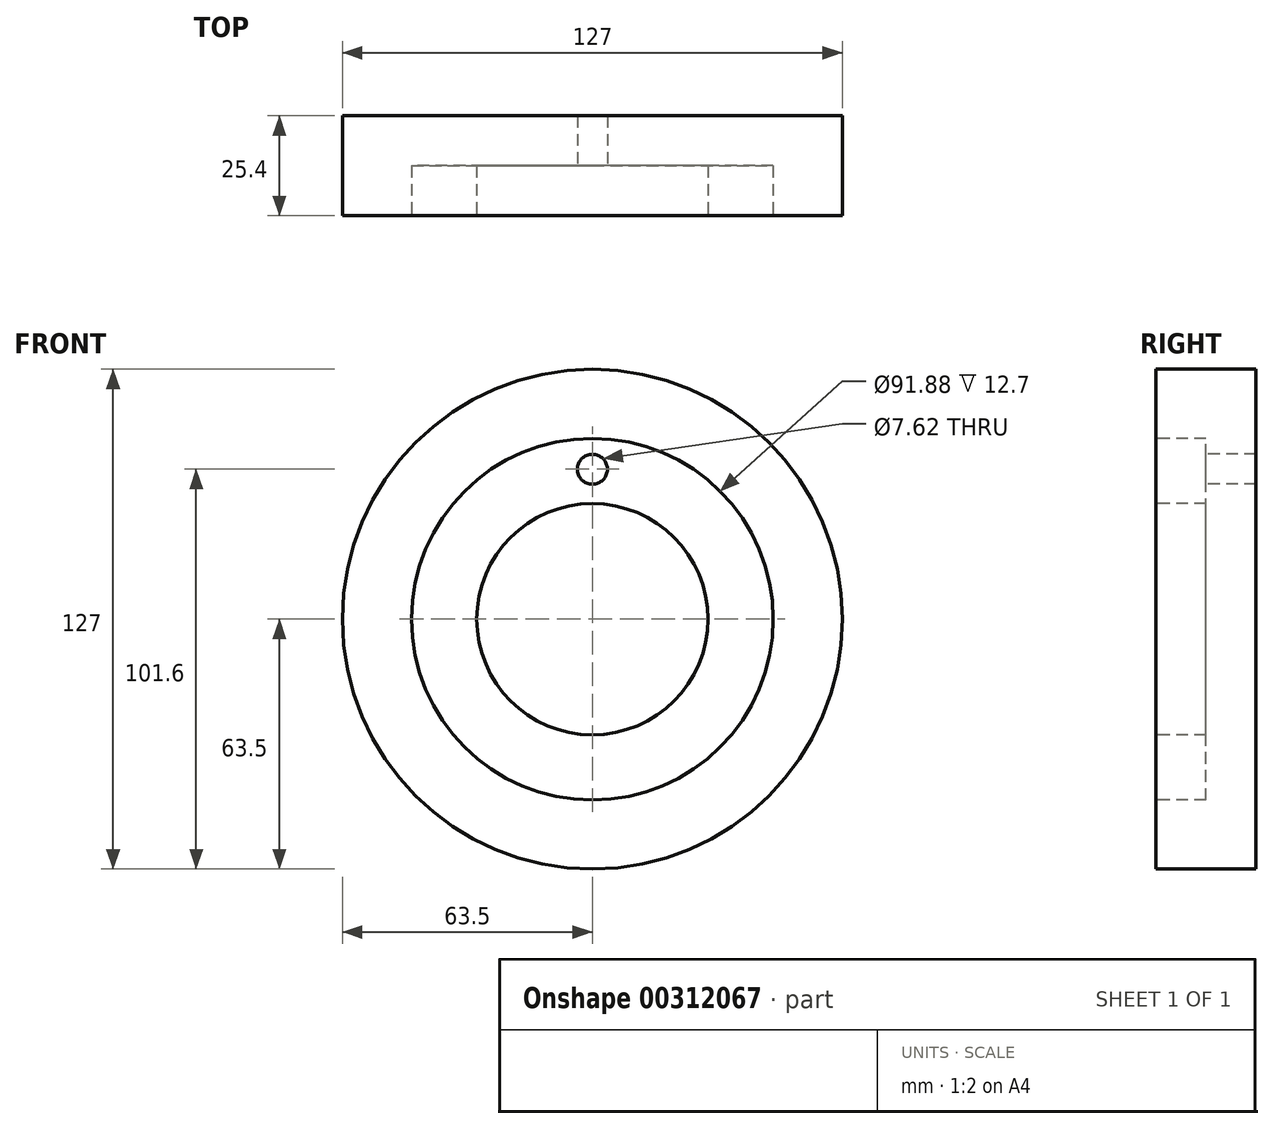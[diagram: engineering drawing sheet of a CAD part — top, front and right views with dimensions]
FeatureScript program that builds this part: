
annotation { "Feature Type Name" : "Feature", "Feature Type Description" : "" }
export const myFeature = defineFeature(function(context is Context, id is Id, definition is map)
    precondition{}
    {
        {
            var Q0;
            Q0=qCreatedBy(makeId("Front.planeOp"),FACE);
            var sketch = newSketch(context, id + "F0", { "sketchPlane" : qUnion([Q0])});
            skCircle(sketch, "E0", {"center": v(0, 0) * mm, "radius": 63.5 * mm});
            skSolve(sketch);
        }
        {
            var Q0;
            Q0 = qSketchRegion(id + "F0", true);
            extrude(context, id + "F1", {"entities" : qUnion([Q0]), "depth" : 25.4 * mm});
        }
        {
            var Q0;
            Q0=makeQuery(id+"F1.opExtrude","CAP_FACE",FACE,{"disambiguationData":[OSD([sQuery(id+"F0.wireOp",EDGE,"E0")])],"isStart":false});
            var sketch = newSketch(context, id + "F2", { "sketchPlane" : qUnion([Q0])});
            skCircle(sketch, "E1", {"center": v(0, 0) * mm, "radius": 45.94 * mm});
            skCircle(sketch, "E2", {"center": v(0, 0) * mm, "radius": 29.37 * mm});
            skSolve(sketch);
        }
        {
            var Q0;
            Q0 = qSketchRegion(id + "F2", true);
            extrude(context, id + "F3", {"entities" : qUnion([Q0]), "operationType" : NewBodyOperationType.REMOVE, "oppositeDirection" : true, "depth" : 12.7 * mm});
        }
        {
            var Q0;
            Q0=makeQuery(id+"F3.boolean.opBoolean","COPY",FACE,{"derivedFrom":makeQuery(id+"F3.opExtrude","CAP_FACE",FACE,{"disambiguationData":[OSD([sQuery(id+"F2.wireOp",EDGE,"E1"),sQuery(id+"F2.wireOp",EDGE,"E2")])],"isStart":false})});
            var sketch = newSketch(context, id + "F4", { "sketchPlane" : qUnion([Q0])});
            skCircle(sketch, "E3", {"center": v(0, 38.1) * mm, "radius": 3.8 * mm});
            skSolve(sketch);
        }
        {
            var Q0;
            Q0 = qSketchRegion(id + "F4", true);
            extrude(context, id + "F5", {"entities" : qUnion([Q0]), "operationType" : NewBodyOperationType.REMOVE, "endBound" : BoundingType.THROUGH_ALL, "oppositeDirection" : true, "depth" : 25.4 * mm});
        }
    });
